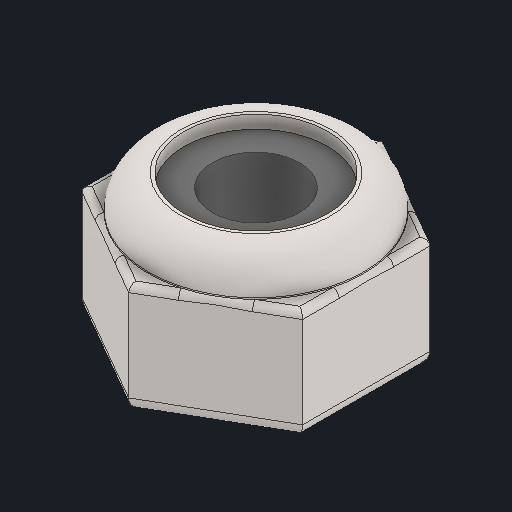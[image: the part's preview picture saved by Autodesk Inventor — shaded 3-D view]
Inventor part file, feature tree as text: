
AUTODESK INVENTOR PART (.ipt)
format: ipt  version: 2024 (Build 280153000, 153)  size: 202,752 bytes
history: native  units: in
note: dims shown in document units (in); Inventor stores cm internally (conversion verified against a paired STEP export)
features: fillet x1
ambient origin geometry x8: Origin, YZ Plane, XZ Plane, XY Plane, X Axis, Y Axis, Z Axis, Center Point
bodies: Solid1 (feature_tree)
feature tree (1):
  fillet  "Fillet6"  [1 undecoded]
note: 1 required parameter value undecoded (feature->parameter linkage not recoverable at this tier; creation-order binding heuristic only, values carry confidence <= 0.55)
